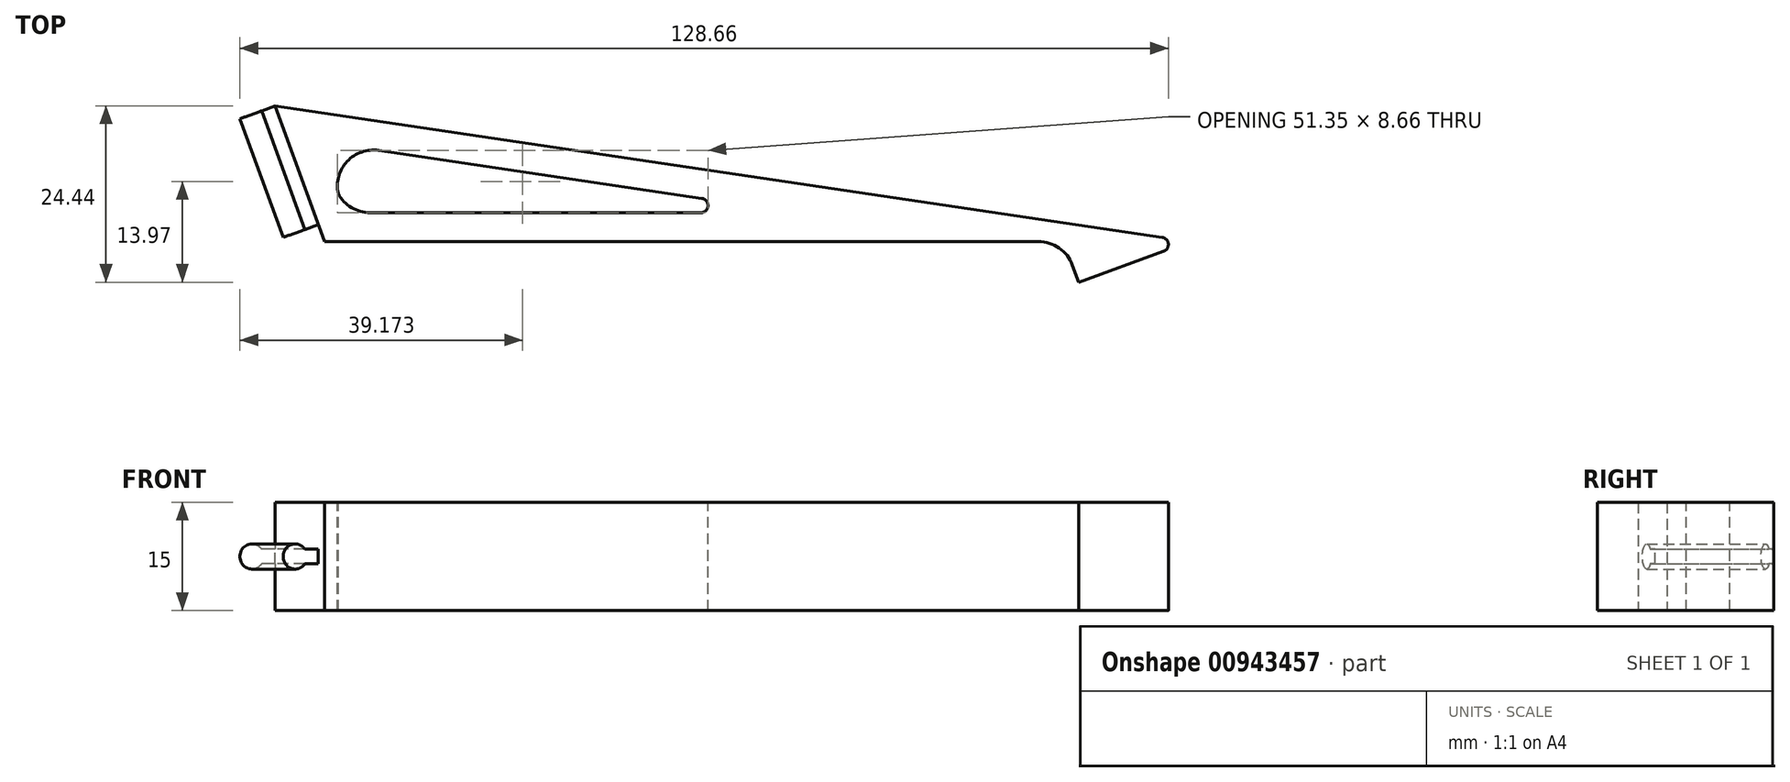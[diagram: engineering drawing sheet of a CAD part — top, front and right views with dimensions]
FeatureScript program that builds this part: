
annotation { "Feature Type Name" : "Feature", "Feature Type Description" : "" }
export const myFeature = defineFeature(function(context is Context, id is Id, definition is map)
    precondition{}
    {
        {
            var Q0;
            Q0=qCreatedBy(makeId("Top.planeOp"),FACE);
            var sketch = newSketch(context, id + "F0", { "sketchPlane" : qUnion([Q0])});
            skLineSegment(sketch, "E0.0", {"start": v(-56.58, -13.76) * mm, "end": v(-63.42, 5.04) * mm});
            skLineSegment(sketch, "E0.1", {"start": v(-63.42, 5.04) * mm, "end": v(63.42, -13.76) * mm});
            skLineSegment(sketch, "E0.2", {"start": v(63.42, -13.76) * mm, "end": v(-56.58, -13.76) * mm});
            skPoint(sketch, "E0.0.midPoint", {"position": v(-60, -4.36) * mm});
            skLineSegment(sketch, "E1.0", {"start": v(9.13, -9.76) * mm, "end": v(-53.78, -9.76) * mm});
            skLineSegment(sketch, "E1.1", {"start": v(-57.37, 0.1) * mm, "end": v(9.13, -9.76) * mm});
            skLineSegment(sketch, "E1.2", {"start": v(-53.78, -9.76) * mm, "end": v(-57.37, 0.1) * mm});
            skLineSegment(sketch, "E2", {"start": v(45.88, -13.76) * mm, "end": v(47.93, -19.4) * mm});
            skLineSegment(sketch, "E3", {"start": v(47.93, -19.4) * mm, "end": v(63.42, -13.76) * mm});
            skSolve(sketch);
        }
        {
            var Q0;
            {var subQ1=sQuery(id+"F0.wireOp",EDGE,"E0.0");Q0=makeQuery(id+"F0.imprint","IMPRINT",FACE,{"disambiguationData":[TD([[makeQuery(id+"F0.imprint","IMPRINT",EDGE,{"derivedFrom":subQ1}),-1.0]])]});}
            var Q1;
            {var subQ2=sQuery(id+"F0.wireOp",EDGE,"E2");Q1=makeQuery(id+"F0.imprint","IMPRINT",FACE,{"disambiguationData":[TD([[makeQuery(id+"F0.imprint","IMPRINT",EDGE,{"derivedFrom":subQ2}),1.0]])]});}
            extrude(context, id + "F1", {"entities" : qUnion([Q0, Q1]), "depth" : 15 * mm, "offsetDistance" : 25 * mm});
        }
        {
            var Q0;
            Q0=makeQuery(id+"F1.opExtrude","SWEPT_EDGE",EDGE,{"disambiguationData":[OSD([sQuery(id+"F0.wireOp",EDGE,"E0.2"),sQuery(id+"F0.wireOp",EDGE,"E2")])]});
            var Q1;
            Q1=makeQuery(id+"F1.opExtrude","SWEPT_EDGE",EDGE,{"disambiguationData":[OSD([sQuery(id+"F0.wireOp",EDGE,"E1.0"),sQuery(id+"F0.wireOp",EDGE,"E1.2")])]});
            var Q2;
            Q2=makeQuery(id+"F1.opExtrude","SWEPT_EDGE",EDGE,{"disambiguationData":[OSD([sQuery(id+"F0.wireOp",EDGE,"E1.1"),sQuery(id+"F0.wireOp",EDGE,"E1.2")])]});
            fillet(context, id + "F2", {"entities" : qUnion([Q0, Q1, Q2]), "radius" : 5 * mm, "tangentPropagation" : true, "allowEdgeOverflow" : false});
        }
        {
            var Q0;
            Q0=makeQuery(id+"F1.opExtrude","SWEPT_EDGE",EDGE,{"disambiguationData":[OSD([sQuery(id+"F0.wireOp",EDGE,"E0.1"),sQuery(id+"F0.wireOp",EDGE,"E0.2"),sQuery(id+"F0.wireOp",EDGE,"E3")])]});
            var Q1;
            Q1=makeQuery(id+"F1.opExtrude","SWEPT_EDGE",EDGE,{"disambiguationData":[OSD([sQuery(id+"F0.wireOp",EDGE,"E1.0"),sQuery(id+"F0.wireOp",EDGE,"E1.1")])]});
            fillet(context, id + "F3", {"entities" : qUnion([Q0, Q1]), "radius" : 1 * mm, "tangentPropagation" : true, "allowEdgeOverflow" : false});
        }
        {
            var Q0;
            Q0=makeQuery(id+"F1.opExtrude","SWEPT_EDGE",EDGE,{"disambiguationData":[OSD([sQuery(id+"F0.wireOp",EDGE,"E0.0"),sQuery(id+"F0.wireOp",EDGE,"E0.1")])]});
            cPlane(context, id + "F4", {"entities" : qUnion([Q0]), "cplaneType" : CPlaneType.LINE_ANGLE, "offset" : 25 * mm, "angle" : 70 * degree, "width" : 150 * mm, "height" : 150 * mm});
        }
        {
            var Q0;
            Q0=qCreatedBy(id+"F4.planeOp",FACE);
            var sketch = newSketch(context, id + "F5", { "sketchPlane" : qUnion([Q0])});
            skLineSegment(sketch, "E4.bottom", {"start": v(57.87, 6.5) * mm, "end": v(59.87, 6.5) * mm});
            skLineSegment(sketch, "E4.top", {"start": v(57.87, 8.5) * mm, "end": v(59.87, 8.5) * mm});
            skLineSegment(sketch, "E4.left", {"start": v(57.87, 6.5) * mm, "end": v(57.87, 8.5) * mm});
            skArc(sketch, "E5", {"start": v(59.87, 6.5) * mm, "mid": v(63.06, 7.5) * mm, "end": v(59.87, 8.5) * mm});
            skSolve(sketch);
        }
        {
            var Q0;
            Q0=makeQuery(id+"F5.imprint","IMPRINT",FACE,{"disambiguationData":[TD([[makeQuery(id+"F5.imprint","IMPRINT",EDGE,{"derivedFrom":sQuery(id+"F5.wireOp",EDGE,"E4.bottom")}),1.0]])]});
            extrude(context, id + "F6", {"entities" : qUnion([Q0]), "operationType" : NewBodyOperationType.ADD, "oppositeDirection" : true, "depth" : 17.5 * mm, "offsetDistance" : 25 * mm});
        }
    });
